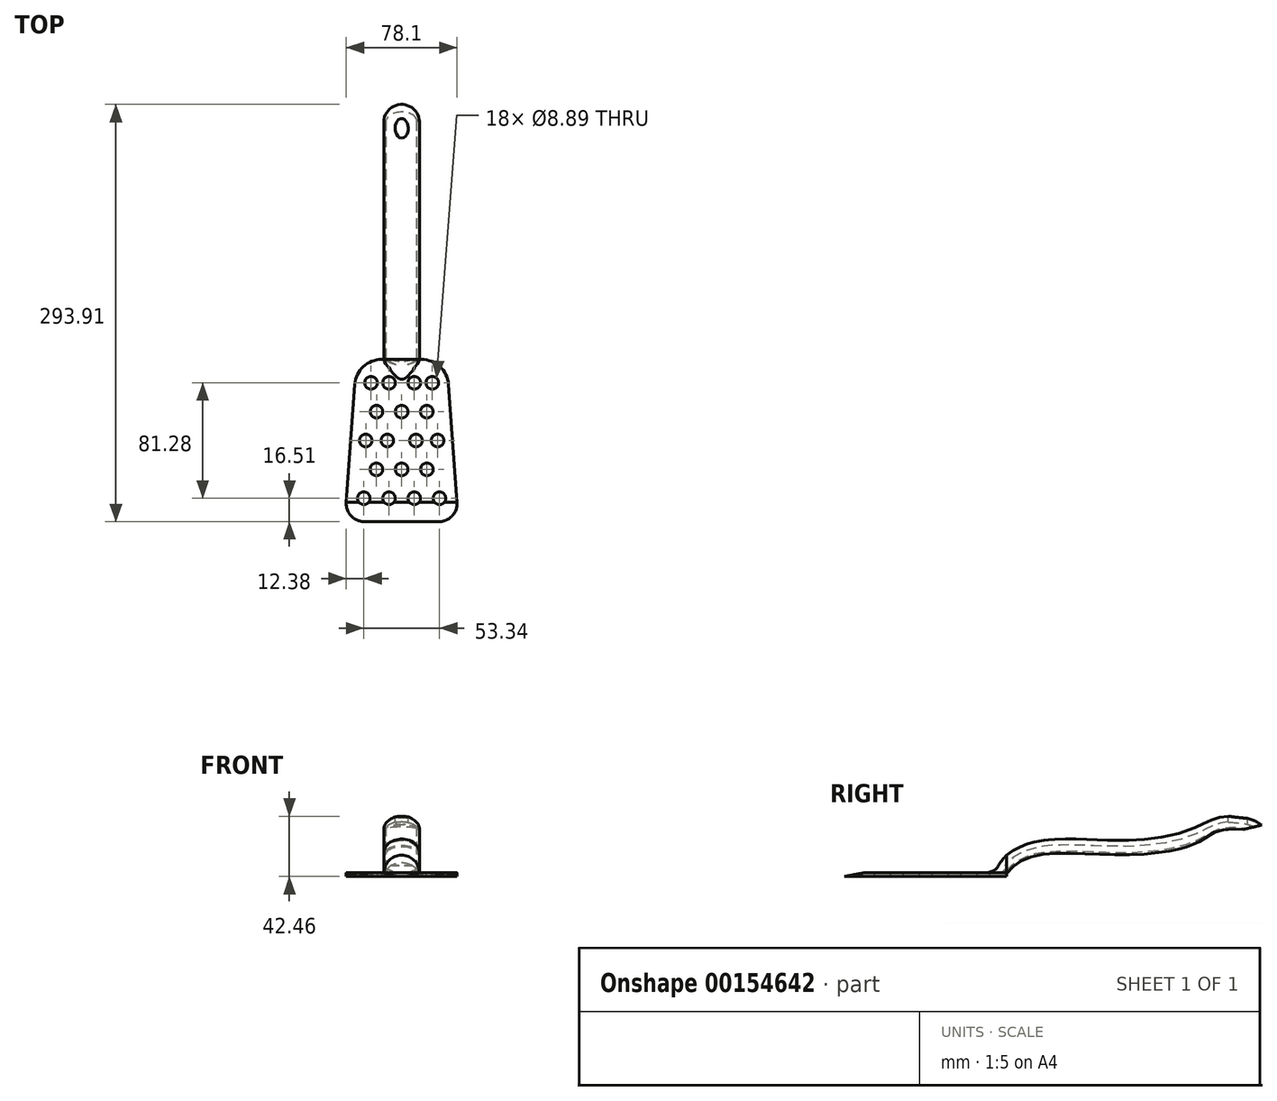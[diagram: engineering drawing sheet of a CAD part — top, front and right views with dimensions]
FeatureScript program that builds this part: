
annotation { "Feature Type Name" : "Feature", "Feature Type Description" : "" }
export const myFeature = defineFeature(function(context is Context, id is Id, definition is map)
    precondition{}
    {
        {
            var Q0;
            Q0=qCreatedBy(makeId("Front.planeOp"),FACE);
            var sketch = newSketch(context, id + "F0", { "sketchPlane" : qUnion([Q0])});
            skArc(sketch, "E0", {"start": v(12.5, -0.1) * mm, "mid": v(0, 12.5) * mm, "end": v(-12.5, -0.1) * mm});
            skEllipticalArc(sketch, "E1", {});
            skPoint(sketch, "E2", {"position": v(0, 7) * mm});
            skPoint(sketch, "E3", {"position": v(11, 0) * mm});
            skLineSegment(sketch, "E4", {"start": v(-11.53, -0.3) * mm, "end": v(-10.48, 2.13) * mm});
            skLineSegment(sketch, "E5.MirrorCS", {"start": v(11.53, -0.3) * mm, "end": v(10.48, 2.13) * mm});
            skPoint(sketch, "E6.visualSharp", {"position": v(-12.32, -2.14) * mm});
            skArc(sketch, "E6.filletArc", {"start": v(-12.5, -0.1) * mm, "mid": v(-12.1, -0.6) * mm, "end": v(-11.53, -0.3) * mm});
            skPoint(sketch, "E7.visualSharp", {"position": v(12.32, -2.14) * mm});
            skArc(sketch, "E7.filletArc", {"start": v(11.53, -0.3) * mm, "mid": v(12.1, -0.6) * mm, "end": v(12.5, -0.1) * mm});
            skPoint(sketch, "E8", {"position": v(0, 12.5) * mm});
            const initialGuessF0  = {"E1": [0, 0, 0, 1, 0.007, 0.011, 4.938687666005643, 1.3444976411739429]};
            skSetInitialGuess(sketch, initialGuessF0);
            skSolve(sketch);
        }
        {
            var Q0;
            Q0=qCreatedBy(makeId("Right.planeOp"),FACE);
            var sketch = newSketch(context, id + "F1", { "sketchPlane" : qUnion([Q0])});
            skLineSegment(sketch, "E9", {"start": v(0, 90.04) * mm, "end": v(180.84, 90.04) * mm});
            skFitSpline(sketch, "E10", {"points": [v(0, 12.5) * mm, v(20.87, 22.08) * mm, v(52.39, 23.7) * mm, v(90.6, 23.19) * mm, v(128.28, 30.02) * mm, v(151.88, 39.44) * mm, v(179.6, 33.66) * mm], "startDerivative": vector(119.53, 98.75) * mm, "endDerivative": vector(136.94, -103.78) * mm});
            skSolve(sketch);
        }
        {
            var Q0;
            Q0=makeQuery(id+"F0.imprint","IMPRINT",FACE,{"disambiguationData":[TD([[makeQuery(id+"F0.imprint","IMPRINT",EDGE,{"derivedFrom":sQuery(id+"F0.wireOp",EDGE,"E0")}),1.0]])]});
            var Q1;
            Q1=sQuery(id+"F1.wireOp",EDGE,"E10");
            sweep(context, id + "F2", {"profiles" : qUnion([Q0]), "path" : qUnion([Q1])});
        }
        {
            var Q0;
            Q0=qCreatedBy(makeId("Front.planeOp"),FACE);
            var sketch = newSketch(context, id + "F3", { "sketchPlane" : qUnion([Q0])});
            skArc(sketch, "E11", {"start": v(12.5, -0.1) * mm, "mid": v(0, 12.5) * mm, "end": v(-12.5, -0.1) * mm});
            skEllipticalArc(sketch, "E12", {});
            skPoint(sketch, "E13", {"position": v(0, 7) * mm});
            skPoint(sketch, "E14", {"position": v(11, 0) * mm});
            skPoint(sketch, "E15.startSnap0", {"position": v(-11, 0) * mm});
            skPoint(sketch, "E15.endSnap0", {"position": v(-11, 0) * mm});
            skLineSegment(sketch, "E16", {"start": v(-11.53, -0.3) * mm, "end": v(-10.36, 2.35) * mm});
            skLineSegment(sketch, "E17.MirrorCS", {"start": v(11.53, -0.3) * mm, "end": v(10.36, 2.35) * mm});
            skArc(sketch, "E18.filletArc", {"start": v(-12.5, -0.1) * mm, "mid": v(-12.1, -0.6) * mm, "end": v(-11.53, -0.3) * mm});
            skArc(sketch, "E19.filletArc", {"start": v(11.53, -0.3) * mm, "mid": v(12.1, -0.6) * mm, "end": v(12.5, -0.1) * mm});
            skPoint(sketch, "E20", {"position": v(0, 12.5) * mm});
            const initialGuessF3  = {"E12": [0, 0, 0, 1, 0.007, 0.011, 4.71238898038469, 1.5707963267948966]};
            skSetInitialGuess(sketch, initialGuessF3);
            skSolve(sketch);
        }
        {
            var Q0;
            Q0=qCreatedBy(makeId("Top.planeOp"),FACE);
            var sketch = newSketch(context, id + "F4", { "sketchPlane" : qUnion([Q0])});
            skLineSegment(sketch, "E21", {"start": v(-14.03, 0) * mm, "end": v(14.03, 0) * mm});
            skLineSegment(sketch, "E22", {"start": v(-33.03, -17.68) * mm, "end": v(-39.02, -100.69) * mm});
            skLineSegment(sketch, "E23", {"start": v(-26.35, -114.3) * mm, "end": v(26.35, -114.3) * mm});
            skLineSegment(sketch, "E24", {"start": v(39.02, -100.69) * mm, "end": v(33.03, -17.68) * mm});
            skPoint(sketch, "E25.visualSharp", {"position": v(-31.75, 0) * mm});
            skArc(sketch, "E25.filletArc", {"start": v(-14.03, 0) * mm, "mid": v(-27, -5.1) * mm, "end": v(-33.03, -17.68) * mm});
            skPoint(sketch, "E26.visualSharp", {"position": v(31.75, 0) * mm});
            skArc(sketch, "E26.filletArc", {"start": v(33.03, -17.68) * mm, "mid": v(27, -5.1) * mm, "end": v(14.03, 0) * mm});
            skPoint(sketch, "E27.visualSharp", {"position": v(-40, -114.3) * mm});
            skArc(sketch, "E27.filletArc", {"start": v(-39.02, -100.69) * mm, "mid": v(-35.65, -110.25) * mm, "end": v(-26.35, -114.3) * mm});
            skPoint(sketch, "E28.visualSharp", {"position": v(40, -114.3) * mm});
            skArc(sketch, "E28.filletArc", {"start": v(26.35, -114.3) * mm, "mid": v(35.65, -110.25) * mm, "end": v(39.02, -100.69) * mm});
            skSolve(sketch);
        }
        {
            var Q0;
            Q0=makeQuery(id+"F4.imprint","IMPRINT",FACE,{"disambiguationData":[TD([[makeQuery(id+"F4.imprint","IMPRINT",EDGE,{"derivedFrom":sQuery(id+"F4.wireOp",EDGE,"E21")}),-1.0]])]});
            extrude(context, id + "F5", {"entities" : qUnion([Q0]), "operationType" : NewBodyOperationType.ADD, "oppositeDirection" : true, "depth" : 2.54 * mm});
        }
        {
            var Q0;
            Q0=makeQuery(id+"F5.opExtrude","CAP_FACE",FACE,{"disambiguationData":[OSD([sQuery(id+"F4.wireOp",EDGE,"E21"),sQuery(id+"F4.wireOp",EDGE,"E22"),sQuery(id+"F4.wireOp",EDGE,"E23"),sQuery(id+"F4.wireOp",EDGE,"E24"),sQuery(id+"F4.wireOp",EDGE,"E25.filletArc"),sQuery(id+"F4.wireOp",EDGE,"E26.filletArc"),sQuery(id+"F4.wireOp",EDGE,"E27.filletArc"),sQuery(id+"F4.wireOp",EDGE,"E28.filletArc")])],"isStart":true});
            var sketch = newSketch(context, id + "F6", { "sketchPlane" : qUnion([Q0])});
            skLineSegment(sketch, "E29", {"start": v(0, 0) * mm, "end": v(0, -14.32) * mm});
            skSolve(sketch);
        }
        {
            var Q0;
            Q0=qCreatedBy(makeId("Right.planeOp"),FACE);
            var sketch = newSketch(context, id + "F7", { "sketchPlane" : qUnion([Q0])});
            skFitSpline(sketch, "E30", {"points": [v(0, 12.5) * mm, v(-6.46, 4.19) * mm, v(-14.18, 0) * mm], "startDerivative": vector(-21.91, -19.02) * mm, "endDerivative": vector(-33.19, -7.79) * mm});
            skSolve(sketch);
        }
        {
            var Q0;
            Q0=makeQuery(id+"F3.imprint","IMPRINT",FACE,{"disambiguationData":[TD([[makeQuery(id+"F3.imprint","IMPRINT",EDGE,{"derivedFrom":sQuery(id+"F3.wireOp",EDGE,"E11")}),1.0]])]});
            var Q1;
            Q1=sQuery(id+"F7.wireOp",EDGE,"E30");
            sweep(context, id + "F8", {"operationType" : NewBodyOperationType.ADD, "profiles" : qUnion([Q0]), "path" : qUnion([Q1])});
        }
        {
            var Q0;
            Q0=qCreatedBy(makeId("Front.planeOp"),FACE);
            var sketch = newSketch(context, id + "F9", { "sketchPlane" : qUnion([Q0])});
            skLineSegment(sketch, "E31.bottom", {"start": v(19.05, -12.35) * mm, "end": v(-19.05, -12.35) * mm});
            skLineSegment(sketch, "E31.top", {"start": v(19.05, -2.54) * mm, "end": v(-19.05, -2.54) * mm});
            skLineSegment(sketch, "E31.left", {"start": v(19.05, -12.35) * mm, "end": v(19.05, -2.54) * mm});
            skLineSegment(sketch, "E31.right", {"start": v(-19.05, -12.35) * mm, "end": v(-19.05, -2.54) * mm});
            skSolve(sketch);
        }
        {
            var Q0;
            Q0 = qSketchRegion(id + "F9", true);
            extrude(context, id + "F10", {"entities" : qUnion([Q0]), "operationType" : NewBodyOperationType.REMOVE, "depth" : 25.4 * mm});
        }
        {
            var Q0;
            Q0=qCreatedBy(makeId("Right.planeOp"),FACE);
            var sketch = newSketch(context, id + "F11", { "sketchPlane" : qUnion([Q0])});
            skLineSegment(sketch, "E32", {"start": v(-100.7, 0) * mm, "end": v(-114.54, -2.54) * mm});
            skLineSegment(sketch, "E33", {"start": v(-100.7, 0) * mm, "end": v(-114.6, 0) * mm});
            skLineSegment(sketch, "E34", {"start": v(-114.6, 0) * mm, "end": v(-114.54, -2.54) * mm});
            skSolve(sketch);
        }
        {
            var Q0;
            Q0 = qSketchRegion(id + "F11", true);
            extrude(context, id + "F12", {"entities" : qUnion([Q0]), "operationType" : NewBodyOperationType.REMOVE, "oppositeDirection" : true, "depth" : 50.8 * mm, "hasSecondDirection" : true, "secondDirectionOppositeDirection" : false, "secondDirectionDepth" : 50.8 * mm});
        }
        {
            var Q0;
            Q0=makeQuery(id+"F10.boolean.opBoolean","MERGE",FACE,{"derivedFrom":[makeQuery(id+"F5.opExtrude","CAP_FACE",FACE,{"disambiguationData":[OSD([sQuery(id+"F4.wireOp",EDGE,"E21"),sQuery(id+"F4.wireOp",EDGE,"E22"),sQuery(id+"F4.wireOp",EDGE,"E23"),sQuery(id+"F4.wireOp",EDGE,"E24"),sQuery(id+"F4.wireOp",EDGE,"E25.filletArc"),sQuery(id+"F4.wireOp",EDGE,"E26.filletArc"),sQuery(id+"F4.wireOp",EDGE,"E27.filletArc"),sQuery(id+"F4.wireOp",EDGE,"E28.filletArc")])],"isStart":false}),makeQuery(id+"F10.opExtrude","SWEPT_FACE",FACE,{"disambiguationData":[OSD([sQuery(id+"F9.wireOp",EDGE,"E31.top")])]})]});
            var sketch = newSketch(context, id + "F13", { "sketchPlane" : qUnion([Q0])});
            skPoint(sketch, "E35.endSnap0", {"position": v(0, 114.3) * mm});
            skCircle(sketch, "E36", {"center": v(-26.67, 97.8) * mm, "radius": 4.45 * mm});
            skCircle(sketch, "E37", {"center": v(-8.9, 97.8) * mm, "radius": 4.45 * mm});
            skCircle(sketch, "E38", {"center": v(-17.78, 77.47) * mm, "radius": 4.45 * mm});
            skCircle(sketch, "E39", {"center": v(-25.32, 57.15) * mm, "radius": 4.45 * mm});
            skCircle(sketch, "E40", {"center": v(-10.08, 57.15) * mm, "radius": 4.45 * mm});
            skCircle(sketch, "E41", {"center": v(-17.7, 36.83) * mm, "radius": 4.45 * mm});
            skCircle(sketch, "E42", {"center": v(-21.6, 16.51) * mm, "radius": 4.45 * mm});
            skCircle(sketch, "E43", {"center": v(-8.9, 16.51) * mm, "radius": 4.45 * mm});
            skCircle(sketch, "E44.MirrorC", {"center": v(8.9, 97.8) * mm, "radius": 4.45 * mm});
            skCircle(sketch, "E45.MirrorC", {"center": v(26.67, 97.8) * mm, "radius": 4.45 * mm});
            skCircle(sketch, "E46.MirrorC", {"center": v(17.78, 77.47) * mm, "radius": 4.45 * mm});
            skCircle(sketch, "E47.MirrorC", {"center": v(10.08, 57.15) * mm, "radius": 4.45 * mm});
            skCircle(sketch, "E48.MirrorC", {"center": v(25.32, 57.15) * mm, "radius": 4.45 * mm});
            skCircle(sketch, "E49.MirrorC", {"center": v(17.7, 36.83) * mm, "radius": 4.45 * mm});
            skCircle(sketch, "E50.MirrorC", {"center": v(8.9, 16.51) * mm, "radius": 4.45 * mm});
            skCircle(sketch, "E51.MirrorC", {"center": v(21.6, 16.51) * mm, "radius": 4.45 * mm});
            skCircle(sketch, "E52", {"center": v(0, 77.47) * mm, "radius": 4.45 * mm});
            skCircle(sketch, "E53", {"center": v(0, 36.83) * mm, "radius": 4.45 * mm});
            skSolve(sketch);
        }
        {
            var Q0;
            Q0 = qSketchRegion(id + "F13", true);
            extrude(context, id + "F14", {"entities" : qUnion([Q0]), "operationType" : NewBodyOperationType.REMOVE, "oppositeDirection" : true, "depth" : 25.4 * mm});
        }
        {
            var Q0;
            Q0=qCreatedBy(makeId("Top.planeOp"),FACE);
            cPlane(context, id + "F15", {"entities" : qUnion([Q0]), "cplaneType" : CPlaneType.OFFSET, "offset" : 50.8 * mm, "width" : 152.4 * mm, "height" : 152.4 * mm});
        }
        {
            var Q0;
            Q0=qCreatedBy(id+"F15.planeOp",FACE);
            var sketch = newSketch(context, id + "F16", { "sketchPlane" : qUnion([Q0])});
            skEllipse(sketch, "E54", {"center": v(0, 162.81) * mm, "majorRadius": 6.86 * mm, "minorRadius": 4.59 * mm, "majorAxis": v(0, -1)});
            skSolve(sketch);
        }
        {
            var Q0;
            Q0 = qSketchRegion(id + "F16", true);
            extrude(context, id + "F17", {"entities" : qUnion([Q0]), "operationType" : NewBodyOperationType.REMOVE, "oppositeDirection" : true, "depth" : 25.4 * mm});
        }
        {
            var Q0;
            {var subQ6=sQuery(id+"F4.wireOp",EDGE,"E22");Q0=makeQuery(id+"F6.imprint","IMPRINT",FACE,{"disambiguationData":[TD([[makeQuery(id+"F6.imprint","IMPRINT",EDGE,{"derivedFrom":makeQuery(id+"F5.opExtrude","CAP_EDGE",EDGE,{"disambiguationData":[OSD([subQ6])],"isStart":true})}),1.0]])]});}
            var sketch = newSketch(context, id + "F18", { "sketchPlane" : qUnion([Q0])});
            skLineSegment(sketch, "E55", {"start": v(0, 0) * mm, "end": v(-10.7, 0) * mm});
            skLineSegment(sketch, "E56", {"start": v(11, 0) * mm, "end": v(-10.7, 0) * mm});
            skFitSpline(sketch, "E57", {"points": [v(-10.7, 0) * mm, v(0, -4.46) * mm, v(11, 0) * mm], "startDerivative": vector(21.44, -13.4) * mm, "endDerivative": vector(21.95, 13.36) * mm});
            skSolve(sketch);
        }
        {
            var Q0;
            Q0 = qSketchRegion(id + "F18", true);
            var Q1;
            Q1=sQuery(id+"F18.wireOp",EDGE,"E56");
            extrude(context, id + "F19", {"entities" : qUnion([Q0]), "operationType" : NewBodyOperationType.ADD, "surfaceEntities" : qUnion([Q1]), "depth" : 5.33 * mm});
        }
        {
            var Q0;
            {var subQ1=sQuery(id+"F4.wireOp",EDGE,"E28.filletArc");var subQ2=sQuery(id+"F4.wireOp",EDGE,"E27.filletArc");var subQ3=sQuery(id+"F4.wireOp",EDGE,"E25.filletArc");var subQ4=sQuery(id+"F4.wireOp",EDGE,"E24");var subQ5=sQuery(id+"F4.wireOp",EDGE,"E26.filletArc");var subQ6=sQuery(id+"F4.wireOp",EDGE,"E21");var subQ7=sQuery(id+"F4.wireOp",EDGE,"E23");var subQ8=sQuery(id+"F4.wireOp",EDGE,"E22");Q0=makeQuery(id+"F8.boolean.opBoolean","SPLIT",FACE,{"disambiguationData":[TD([makeQuery(id+"F5.opExtrude","SWEPT_FACE",FACE,{"disambiguationData":[OSD([subQ8])]})])],"derivedFrom":makeQuery(id+"F5.opExtrude","CAP_FACE",FACE,{"disambiguationData":[OSD([subQ6,subQ8,subQ7,subQ4,subQ3,subQ5,subQ2,subQ1])],"isStart":true})});}
            var sketch = newSketch(context, id + "F20", { "sketchPlane" : qUnion([Q0])});
            skLineSegment(sketch, "E58", {"start": v(-7.03, 0) * mm, "end": v(7.07, 0) * mm});
            skFitSpline(sketch, "E59", {"points": [v(-7.03, 0) * mm, v(0, -1.3) * mm, v(7.07, 0) * mm], "startDerivative": vector(14.06, -3.9) * mm, "endDerivative": vector(14.13, 3.9) * mm});
            skPoint(sketch, "E60.orphan", {"position": v(-10.47, 0) * mm});
            skSolve(sketch);
        }
        {
            var Q0;
            Q0 = qSketchRegion(id + "F20", true);
            extrude(context, id + "F21", {"entities" : qUnion([Q0]), "operationType" : NewBodyOperationType.ADD, "depth" : 7.11 * mm});
        }
    });
